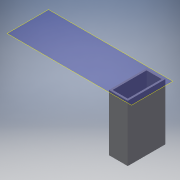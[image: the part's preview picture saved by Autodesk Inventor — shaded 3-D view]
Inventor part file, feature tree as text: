
AUTODESK INVENTOR PART (.ipt)
format: ipt  version: 2018 (Build 220112000, 112)  size: 119,808 bytes
history: native  units: in
note: dims shown in document units (in); Inventor stores cm internally (conversion verified against a paired STEP export)
features: extrude x2, sketch x2, other x2, plane x1
ambient origin geometry x8: Origin, YZ Plane, XZ Plane, XY Plane, X Axis, Y Axis, Z Axis, Center Point
bodies: Solid1 (feature_tree)
feature tree (7):
  plane  "Work Plane1"
  extrude  "Extrusion1"  Depth=2.0in
  extrude  "Extrusion2"  Depth=0.1in
  sketch  "Sketch1"  dims[d0=1.0in d1=2.0in]
  sketch  "Sketch2"  dims[d3=0.1in d4=0.1in d5=0.1in d6=0.1in d7=3.0in d8=0.0in d9=0.5in d10=1.0in d11=0.2031in d12=0.2031in d13=0.5in d14=0.5in d15=3.0in d16=0.0in]
  other  "non integrated hatch.iam"
  other  "left arm:1"
